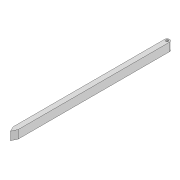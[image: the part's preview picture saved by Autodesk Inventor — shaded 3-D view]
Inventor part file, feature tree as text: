
AUTODESK INVENTOR PART (.ipt)
format: ipt  version: 2022 (Build 260153000, 153)  size: 124,928 bytes
history: native  units: mm
features: extrude x2, sketch x2, projected_geometry x1
ambient origin geometry x8: Origin, YZ Plane, XZ Plane, XY Plane, X Axis, Y Axis, Z Axis, Center Point
bodies: Solid1 (feature_tree)
feature tree (5):
  extrude  "Extrusion1"  Depth=441.93mm
  extrude  "Extrusion2"  Depth=3.0mm
  sketch  "Sketch1"  dims[d0=6.0mm d1=441.93mm]
  sketch  "Sketch2"  dims[d2=3.0mm d3=3.0mm d4=10.0mm d5=0.0mm d20=3.0mm d21=48.203mm d22=3.0mm d23=166.766mm d24=400.0mm d25=400.0mm d26=3.0mm d28=3.0mm d29=4.363323mm d30=4.363323mm d31=100.0mm d32=0.0mm]
  projected_geometry  "Projected Loop1"
